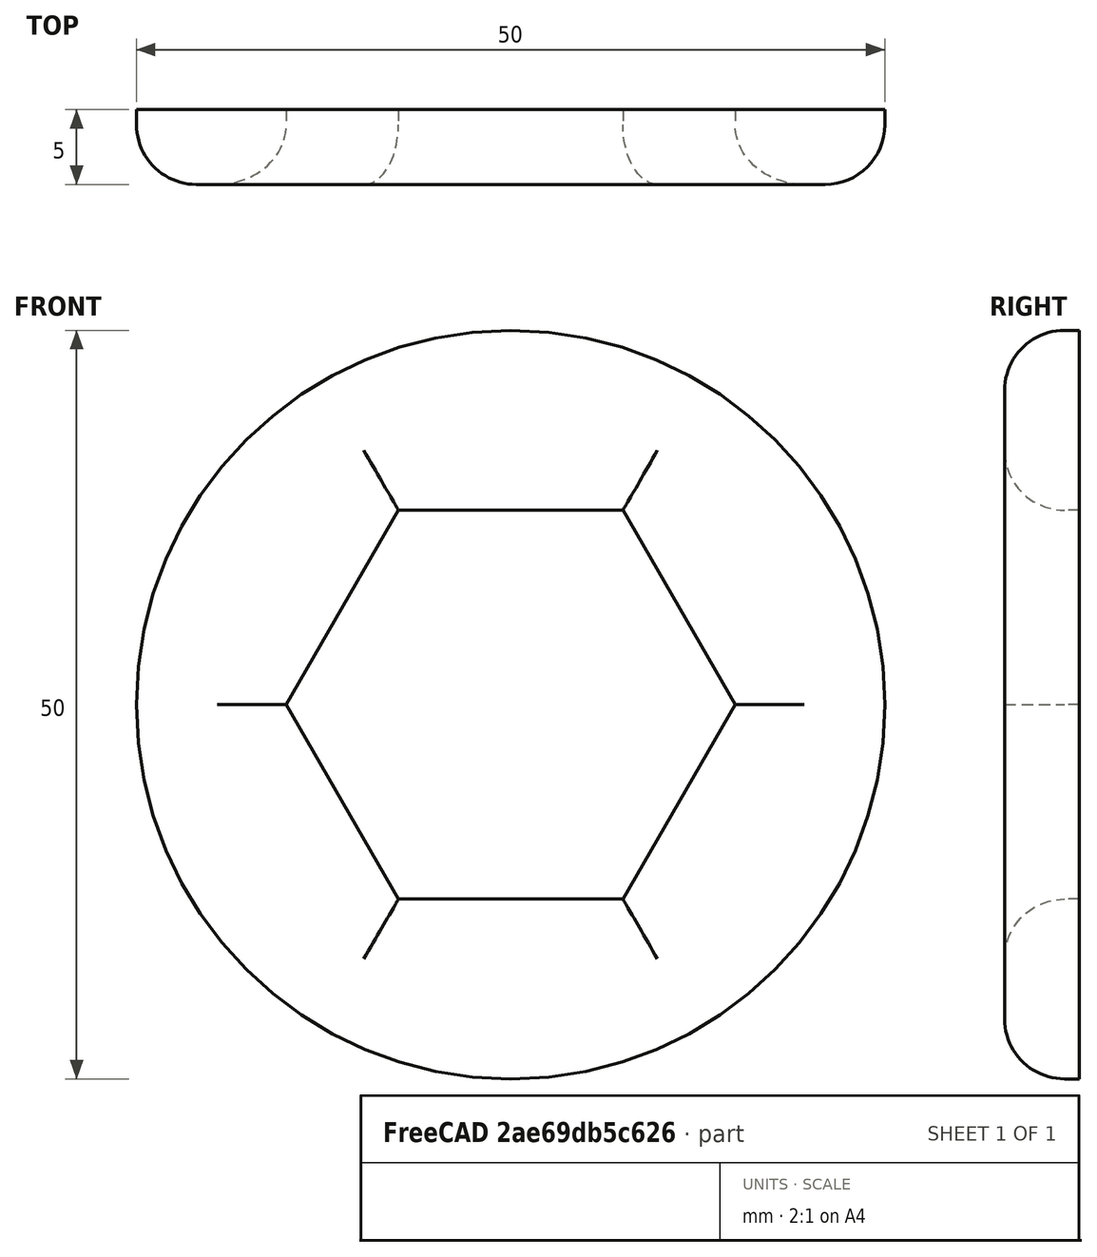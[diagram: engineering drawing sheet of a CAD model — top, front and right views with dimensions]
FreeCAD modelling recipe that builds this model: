
FCSTD DOCUMENT  (FreeCAD 0.19R)
Label: box_panel
License: CreativeCommons Attribution-ShareAlike
LicenseURL: http://creativecommons.org/licenses/by-sa/4.0/
objects: PartDesign::SubShapeBinder×2, PartDesign::Pad×1, PartDesign::Pocket×1, PartDesign::Fillet×1, PartDesign::Body×1, Part::Feature×1, App::Part×1
note: 9 computed .brp shape members not serialized (recipe doc carries the construction recipe); baked Part::Feature solids carry a one-line shape summary decoded from their .brp
EXTERNAL_REF file=base_dimensions.FCStd obj=Part
EXTERNAL_REF file=base_dimensions.FCStd obj=Sketch001

FEATURE [PartDesign::SubShapeBinder] Binder  label="Binder_box_outline"
  BindMode = 0
  ClaimChildren = false
  Context = -> Part [Body.Binder.]
  Fuse = false
  MakeFace = true
  PartialLoad = false
  Relative = true
  Support = -> [<external base_dimensions.FCStd>#Part[Body001.Sketch003.]]
  _Version = 1
FEATURE [PartDesign::SubShapeBinder] Binder001  label="Binder_box_cutout"
  BindMode = 0
  ClaimChildren = false
  Context = -> Part [Body.Binder001.]
  Fuse = false
  MakeFace = true
  PartialLoad = false
  Relative = true
  Support = -> [<external base_dimensions.FCStd>#Part[Body001.Sketch002.]]
  _Version = 1
FEATURE [PartDesign::Pad] Pad
  Length = 5
  Length2 = 100
  Profile = -> Binder [Face1]
  Reversed = true
  Type = 0
  expr: Length = <<base_dimensions>>#<<front_y>>.Constraints.deco_thickness
FEATURE [PartDesign::Pocket] Pocket
  BaseFeature = -> Pad
  Length = 5
  Length2 = 100
  Profile = -> Binder001 [Face1]
  Type = 1
FEATURE [PartDesign::Fillet] Fillet
  Base = -> Pocket [Face3]
  BaseFeature = -> Pocket
  Radius = 4
FEATURE [PartDesign::Body] Body  label="box_panel_body"
  Group = -> [Binder,Binder001,Pad,Pocket,Fillet]
  Origin = -> Origin001
  Tip = -> Fillet
FEATURE [Part::Feature] Body__sc_export  label="box_panel_body__sc_export"
  shape: bbox 54.12 x 5 x 54.12 mm, 16 faces (baked)
FEATURE [App::Part] Part  label="box_panel_part"
  Group = -> [Body,Body__sc_export]
  Origin = -> Origin
